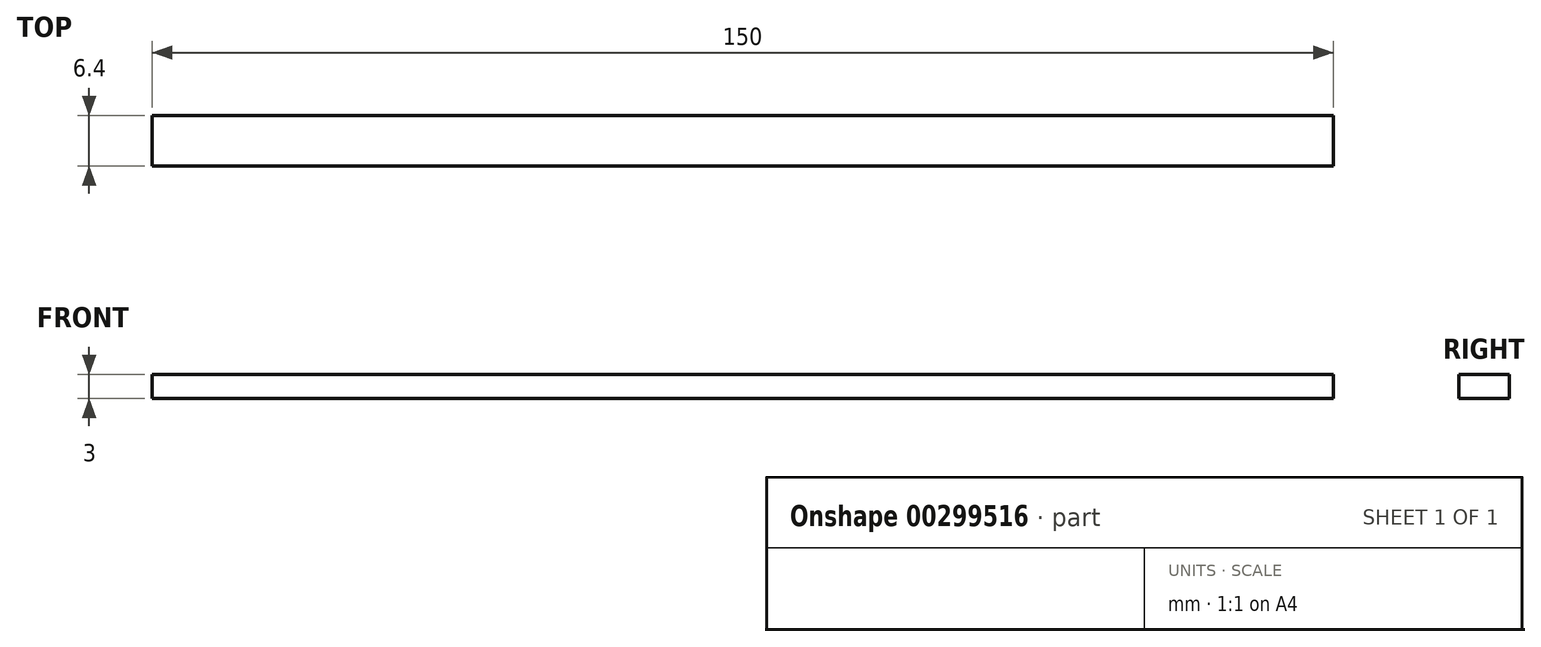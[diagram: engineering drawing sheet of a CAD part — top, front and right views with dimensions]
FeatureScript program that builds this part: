
annotation { "Feature Type Name" : "Feature", "Feature Type Description" : "" }
export const myFeature = defineFeature(function(context is Context, id is Id, definition is map)
    precondition{}
    {
        {
            var Q0;
            Q0=qCreatedBy(makeId("Top.planeOp"),FACE);
            var sketch = newSketch(context, id + "F0", { "sketchPlane" : qUnion([Q0])});
            skLineSegment(sketch, "E0.bottom", {"start": v(75, 3.2) * mm, "end": v(-75, 3.2) * mm});
            skLineSegment(sketch, "E0.top", {"start": v(75, -3.2) * mm, "end": v(-75, -3.2) * mm});
            skLineSegment(sketch, "E0.left", {"start": v(75, 3.2) * mm, "end": v(75, -3.2) * mm});
            skLineSegment(sketch, "E0.right", {"start": v(-75, 3.2) * mm, "end": v(-75, -3.2) * mm});
            skPoint(sketch, "E0.middle", {"position": v(0, 0) * mm});
            skSolve(sketch);
        }
        {
            var Q0;
            Q0=makeQuery(id+"F0.imprint","IMPRINT",FACE,{"disambiguationData":[TD([[makeQuery(id+"F0.imprint","IMPRINT",EDGE,{"derivedFrom":sQuery(id+"F0.wireOp",EDGE,"E0.bottom")}),1.0]])]});
            extrude(context, id + "F1", {"entities" : qUnion([Q0]), "depth" : 3 * mm});
        }
    });
